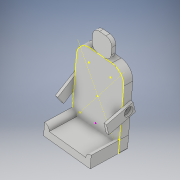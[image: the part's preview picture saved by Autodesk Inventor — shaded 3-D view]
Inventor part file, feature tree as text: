
AUTODESK INVENTOR PART (.ipt)
format: ipt  version: 2018 (Build 220112000, 112)  size: 182,784 bytes
history: native  units: in
note: dims shown in document units (in); Inventor stores cm internally (conversion verified against a paired STEP export)
features: other x6, sketch x5
ambient origin geometry x8: Origin, YZ Plane, XZ Plane, XY Plane, X Axis, Y Axis, Z Axis, Center Point
bodies: Solid7 (feature_tree), Solid8 (feature_tree), Solid9 (feature_tree), Solid10 (feature_tree), Solid11 (feature_tree)
feature tree (11):
  other  "Seat_assembly.iam"
  other  "Seat upper.ipt:1"
  other  "Seat head.ipt:2"
  other  "Seat lower.ipt:1"
  other  "handle.ipt:1"
  other  "handle.ipt:2"
  sketch  "Sketch1"  dims[d1=0.3937in]
  sketch  "Sketch3"
  sketch  "Sketch6"
  sketch  "Sketch12"
  sketch  "Sketch2"
